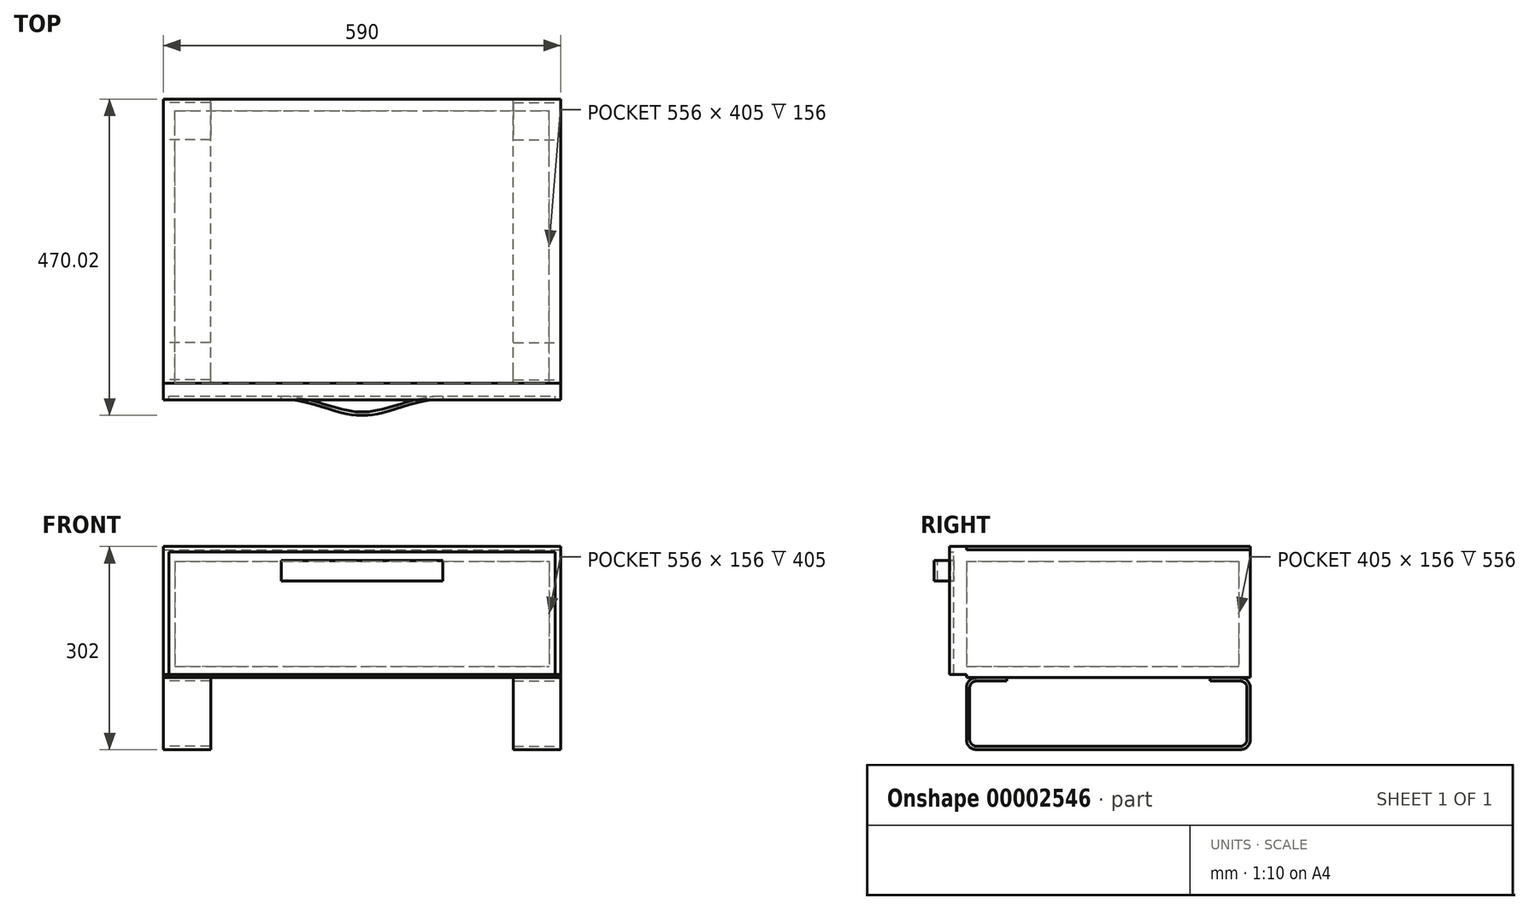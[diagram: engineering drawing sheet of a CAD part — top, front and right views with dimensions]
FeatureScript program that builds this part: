
annotation { "Feature Type Name" : "Feature", "Feature Type Description" : "" }
export const myFeature = defineFeature(function(context is Context, id is Id, definition is map)
    precondition{}
    {
        {
            var Q0;
            Q0=qCreatedBy(makeId("Top.planeOp"),FACE);
            var sketch = newSketch(context, id + "F0", { "sketchPlane" : qUnion([Q0])});
            skLineSegment(sketch, "E0.bottom", {"start": v(0, 0) * mm, "end": v(590, 0) * mm});
            skLineSegment(sketch, "E0.top", {"start": v(0, 422) * mm, "end": v(590, 422) * mm});
            skLineSegment(sketch, "E0.left", {"start": v(0, 0) * mm, "end": v(0, 422) * mm});
            skLineSegment(sketch, "E0.right", {"start": v(590, 0) * mm, "end": v(590, 422) * mm});
            skSolve(sketch);
        }
        {
            var Q0;
            Q0=makeQuery(id+"F0.imprint","IMPRINT",FACE,{"disambiguationData":[TD([[makeQuery(id+"F0.imprint","IMPRINT",EDGE,{"derivedFrom":sQuery(id+"F0.wireOp",EDGE,"E0.bottom")}),1.0]])]});
            extrude(context, id + "F1", {"entities" : qUnion([Q0]), "depth" : 190 * mm});
        }
        {
            var Q0;
            Q0=makeQuery(id+"F1.opExtrude","SWEPT_FACE",FACE,{"disambiguationData":[OSD([sQuery(id+"F0.wireOp",EDGE,"E0.bottom")])]});
            shell(context, id + "F2", {"entities" : qUnion([Q0]), "thickness" : 17 * mm});
        }
        {
            var Q0;
            Q0=qCreatedBy(makeId("Front.planeOp"),FACE);
            var sketch = newSketch(context, id + "F3", { "sketchPlane" : qUnion([Q0])});
            skLineSegment(sketch, "E1.bottom", {"start": v(0, 5) * mm, "end": v(590, 5) * mm});
            skLineSegment(sketch, "E1.top", {"start": v(0, 195) * mm, "end": v(590, 195) * mm});
            skLineSegment(sketch, "E1.left", {"start": v(0, 5) * mm, "end": v(0, 195) * mm});
            skLineSegment(sketch, "E1.right", {"start": v(590, 5) * mm, "end": v(590, 195) * mm});
            skLineSegment(sketch, "E2.0", {"start": v(582, 5) * mm, "end": v(582, 187) * mm});
            skLineSegment(sketch, "E2.1", {"start": v(8, 187) * mm, "end": v(582, 187) * mm});
            skLineSegment(sketch, "E2.2", {"start": v(8, 5) * mm, "end": v(8, 187) * mm});
            skSolve(sketch);
        }
        {
            var Q0;
            {var subQ1=sQuery(id+"F3.wireOp",EDGE,"E2.0");Q0=makeQuery(id+"F3.imprint","IMPRINT",FACE,{"disambiguationData":[TD([[makeQuery(id+"F3.imprint","IMPRINT",EDGE,{"derivedFrom":subQ1}),1.0]])]});}
            extrude(context, id + "F4", {"entities" : qUnion([Q0]), "depth" : 19 * mm});
        }
        {
            var Q0;
            Q0=makeQuery(id+"F3.imprint","IMPRINT",FACE,{"disambiguationData":[TD([[makeQuery(id+"F3.imprint","IMPRINT",EDGE,{"derivedFrom":sQuery(id+"F3.wireOp",EDGE,"E1.top")}),-1.0]])]});
            extrude(context, id + "F5", {"entities" : qUnion([Q0]), "operationType" : NewBodyOperationType.ADD, "depth" : 25 * mm});
        }
        {
            var Q0;
            Q0=makeQuery(id+"F1.opExtrude","CAP_FACE",FACE,{"disambiguationData":[OSD([sQuery(id+"F0.wireOp",EDGE,"E0.bottom"),sQuery(id+"F0.wireOp",EDGE,"E0.top"),sQuery(id+"F0.wireOp",EDGE,"E0.left"),sQuery(id+"F0.wireOp",EDGE,"E0.right")])],"isStart":false});
            extrude(context, id + "F6", {"entities" : qUnion([Q0]), "depth" : 5 * mm});
        }
        {
            var Q0;
            Q0=makeQuery(id+"F4.opExtrude","CAP_FACE",FACE,{"disambiguationData":[OSD([sQuery(id+"F3.wireOp",EDGE,"E1.bottom"),sQuery(id+"F3.wireOp",EDGE,"E2.0"),sQuery(id+"F3.wireOp",EDGE,"E2.1"),sQuery(id+"F3.wireOp",EDGE,"E2.2")])],"isStart":false});
            var sketch = newSketch(context, id + "F7", { "sketchPlane" : qUnion([Q0])});
            skLineSegment(sketch, "E3.bottom", {"start": v(175, 174) * mm, "end": v(415, 174) * mm, "construction": true});
            skLineSegment(sketch, "E3.top", {"start": v(175, 144) * mm, "end": v(415, 144) * mm, "construction": true});
            skLineSegment(sketch, "E3.left", {"start": v(175, 174) * mm, "end": v(175, 144) * mm, "construction": true});
            skLineSegment(sketch, "E3.right", {"start": v(415, 174) * mm, "end": v(415, 144) * mm, "construction": true});
            skLineSegment(sketch, "E4", {"start": v(295, 5) * mm, "end": v(295, 144) * mm, "construction": true});
            skSolve(sketch);
        }
        {
            var Q0;
            Q0=sQuery(id+"F7.wireOp",EDGE,"E3.top");
            cPlane(context, id + "F8", {"entities" : qUnion([Q0]), "cplaneType" : CPlaneType.LINE_ANGLE, "offset" : 150 * mm, "angle" : 90 * degree, "width" : 150 * mm, "height" : 150 * mm});
        }
        {
            var Q0;
            Q0=qCreatedBy(id+"F8.planeOp",FACE);
            var sketch = newSketch(context, id + "F9", { "sketchPlane" : qUnion([Q0])});
            skLineSegment(sketch, "E5.0", {"start": v(175, -19) * mm, "end": v(415, -19) * mm, "construction": true});
            skFitSpline(sketch, "E6", {"points": [v(175, -19) * mm, v(295, -43) * mm, v(415, -19) * mm], "startDerivative": vector(270, 0) * mm, "endDerivative": vector(270, 0) * mm});
            skLineSegment(sketch, "E7", {"start": v(295, -19) * mm, "end": v(295, -43) * mm, "construction": true});
            skFitSpline(sketch, "E8.0", {"points": [v(175, -24) * mm, v(180.4, -24) * mm, v(191.01, -24.72) * mm, v(206.47, -27.45) * mm, v(221.56, -31.31) * mm, v(236.38, -35.77) * mm, v(251.03, -40.3) * mm, v(263.17, -43.63) * mm, v(272.9, -45.75) * mm, v(280.23, -47) * mm, v(286.36, -47.67) * mm, v(291.29, -47.95) * mm, v(295, -48.02) * mm, v(298.71, -47.95) * mm, v(303.64, -47.67) * mm, v(309.77, -47) * mm, v(317.1, -45.75) * mm, v(326.83, -43.63) * mm, v(338.97, -40.3) * mm, v(353.62, -35.77) * mm, v(368.44, -31.31) * mm, v(383.53, -27.45) * mm, v(398.99, -24.72) * mm, v(409.6, -24) * mm, v(415, -24) * mm]});
            skLineSegment(sketch, "E9", {"start": v(175, -24) * mm, "end": v(175, -19) * mm});
            skLineSegment(sketch, "E10", {"start": v(415, -19) * mm, "end": v(415, -24) * mm});
            skSolve(sketch);
        }
        {
            var Q0;
            Q0=makeQuery(id+"F9.imprint","IMPRINT",FACE,{"disambiguationData":[TD([[makeQuery(id+"F9.imprint","IMPRINT",EDGE,{"derivedFrom":sQuery(id+"F9.wireOp",EDGE,"E6")}),-1.0]])]});
            extrude(context, id + "F10", {"entities" : qUnion([Q0]), "depth" : 30 * mm});
        }
        {
            var Q0;
            Q0=qCreatedBy(makeId("Right.planeOp"),FACE);
            var sketch = newSketch(context, id + "F11", { "sketchPlane" : qUnion([Q0])});
            skLineSegment(sketch, "E11.0", {"start": v(0, 0) * mm, "end": v(422, 0) * mm, "construction": true});
            skLineSegment(sketch, "E12.top", {"start": v(15, -107) * mm, "end": v(407, -107) * mm});
            skLineSegment(sketch, "E12.left", {"start": v(0, -15) * mm, "end": v(0, -92) * mm});
            skLineSegment(sketch, "E12.right", {"start": v(422, -15) * mm, "end": v(422, -92) * mm});
            skLineSegment(sketch, "E13", {"start": v(0, 0) * mm, "end": v(60, 0) * mm, "construction": true});
            skLineSegment(sketch, "E14", {"start": v(407, 0) * mm, "end": v(362, 0) * mm});
            skLineSegment(sketch, "E15", {"start": v(15, 0) * mm, "end": v(60, 0) * mm});
            skPoint(sketch, "E16.visualSharp", {"position": v(0, 0) * mm});
            skArc(sketch, "E16.filletArc", {"start": v(15, 0) * mm, "mid": v(4.4, -4.4) * mm, "end": v(0, -15) * mm});
            skPoint(sketch, "E17.visualSharp", {"position": v(0, -107) * mm});
            skArc(sketch, "E17.filletArc", {"start": v(0, -92) * mm, "mid": v(4.4, -102.6) * mm, "end": v(15, -107) * mm});
            skPoint(sketch, "E18.visualSharp", {"position": v(422, 0) * mm});
            skArc(sketch, "E18.filletArc", {"start": v(422, -15) * mm, "mid": v(417.6, -4.4) * mm, "end": v(407, 0) * mm});
            skPoint(sketch, "E19.visualSharp", {"position": v(422, -107) * mm});
            skArc(sketch, "E19.filletArc", {"start": v(407, -107) * mm, "mid": v(417.6, -102.6) * mm, "end": v(422, -92) * mm});
            skLineSegment(sketch, "E20.0", {"start": v(15, -5) * mm, "end": v(60, -5) * mm});
            skArc(sketch, "E20.1", {"start": v(15, -5) * mm, "mid": v(7.93, -7.93) * mm, "end": v(5, -15) * mm});
            skLineSegment(sketch, "E20.2", {"start": v(5, -15) * mm, "end": v(5, -92) * mm});
            skArc(sketch, "E20.3", {"start": v(5, -92) * mm, "mid": v(7.93, -99.07) * mm, "end": v(15, -102) * mm});
            skLineSegment(sketch, "E20.4", {"start": v(15, -102) * mm, "end": v(407, -102) * mm});
            skArc(sketch, "E20.5", {"start": v(407, -102) * mm, "mid": v(414.07, -99.07) * mm, "end": v(417, -92) * mm});
            skLineSegment(sketch, "E20.6", {"start": v(417, -15) * mm, "end": v(417, -92) * mm});
            skArc(sketch, "E20.7", {"start": v(417, -15) * mm, "mid": v(414.07, -7.93) * mm, "end": v(407, -5) * mm});
            skLineSegment(sketch, "E20.8", {"start": v(407, -5) * mm, "end": v(362, -5) * mm});
            skLineSegment(sketch, "E21", {"start": v(60, -5) * mm, "end": v(60, 0) * mm});
            skLineSegment(sketch, "E22", {"start": v(362, -5) * mm, "end": v(362, 0) * mm});
            skSolve(sketch);
        }
        {
            var Q0;
            Q0=makeQuery(id+"F11.imprint","IMPRINT",FACE,{"disambiguationData":[TD([[makeQuery(id+"F11.imprint","IMPRINT",EDGE,{"derivedFrom":sQuery(id+"F11.wireOp",EDGE,"E12.top")}),1.0]])]});
            extrude(context, id + "F12", {"entities" : qUnion([Q0]), "depth" : 70 * mm});
        }
        {
            var Q0;
            Q0=makeQuery(id+"F1.opExtrude","CAP_FACE",FACE,{"disambiguationData":[OSD([sQuery(id+"F0.wireOp",EDGE,"E0.bottom"),sQuery(id+"F0.wireOp",EDGE,"E0.top"),sQuery(id+"F0.wireOp",EDGE,"E0.left"),sQuery(id+"F0.wireOp",EDGE,"E0.right")])],"isStart":true});
            var sketch = newSketch(context, id + "F13", { "sketchPlane" : qUnion([Q0])});
            skLineSegment(sketch, "E23", {"start": v(295, -422) * mm, "end": v(295, 0) * mm, "construction": true});
            skSolve(sketch);
        }
        {
            var Q0;
            Q0=sQuery(id+"F13.wireOp",EDGE,"E23");
            cPlane(context, id + "F14", {"entities" : qUnion([Q0]), "cplaneType" : CPlaneType.LINE_ANGLE, "offset" : 150 * mm, "angle" : 90 * degree, "width" : 150 * mm, "height" : 150 * mm});
        }
        {
            var Q0;
            Q0=makeQuery(id+"F12.opExtrude","SWEPT_BODY",BODY,{"disambiguationData":[OSD([sQuery(id+"F11.wireOp",EDGE,"E12.top"),sQuery(id+"F11.wireOp",EDGE,"E12.left"),sQuery(id+"F11.wireOp",EDGE,"E12.right"),sQuery(id+"F11.wireOp",EDGE,"E14"),sQuery(id+"F11.wireOp",EDGE,"E15"),sQuery(id+"F11.wireOp",EDGE,"E16.filletArc"),sQuery(id+"F11.wireOp",EDGE,"E17.filletArc"),sQuery(id+"F11.wireOp",EDGE,"E18.filletArc"),sQuery(id+"F11.wireOp",EDGE,"E19.filletArc"),sQuery(id+"F11.wireOp",EDGE,"E20.0"),sQuery(id+"F11.wireOp",EDGE,"E20.1"),sQuery(id+"F11.wireOp",EDGE,"E20.2"),sQuery(id+"F11.wireOp",EDGE,"E20.3"),sQuery(id+"F11.wireOp",EDGE,"E20.4"),sQuery(id+"F11.wireOp",EDGE,"E20.5"),sQuery(id+"F11.wireOp",EDGE,"E20.6"),sQuery(id+"F11.wireOp",EDGE,"E20.7"),sQuery(id+"F11.wireOp",EDGE,"E20.8"),sQuery(id+"F11.wireOp",EDGE,"E21"),sQuery(id+"F11.wireOp",EDGE,"E22")])]});
            var Q1;
            Q1=qCreatedBy(id+"F14.planeOp",FACE);
            mirror(context, id + "F15", {"entities" : qUnion([Q0]), "mirrorPlane" : qUnion([Q1])});
        }
    });
